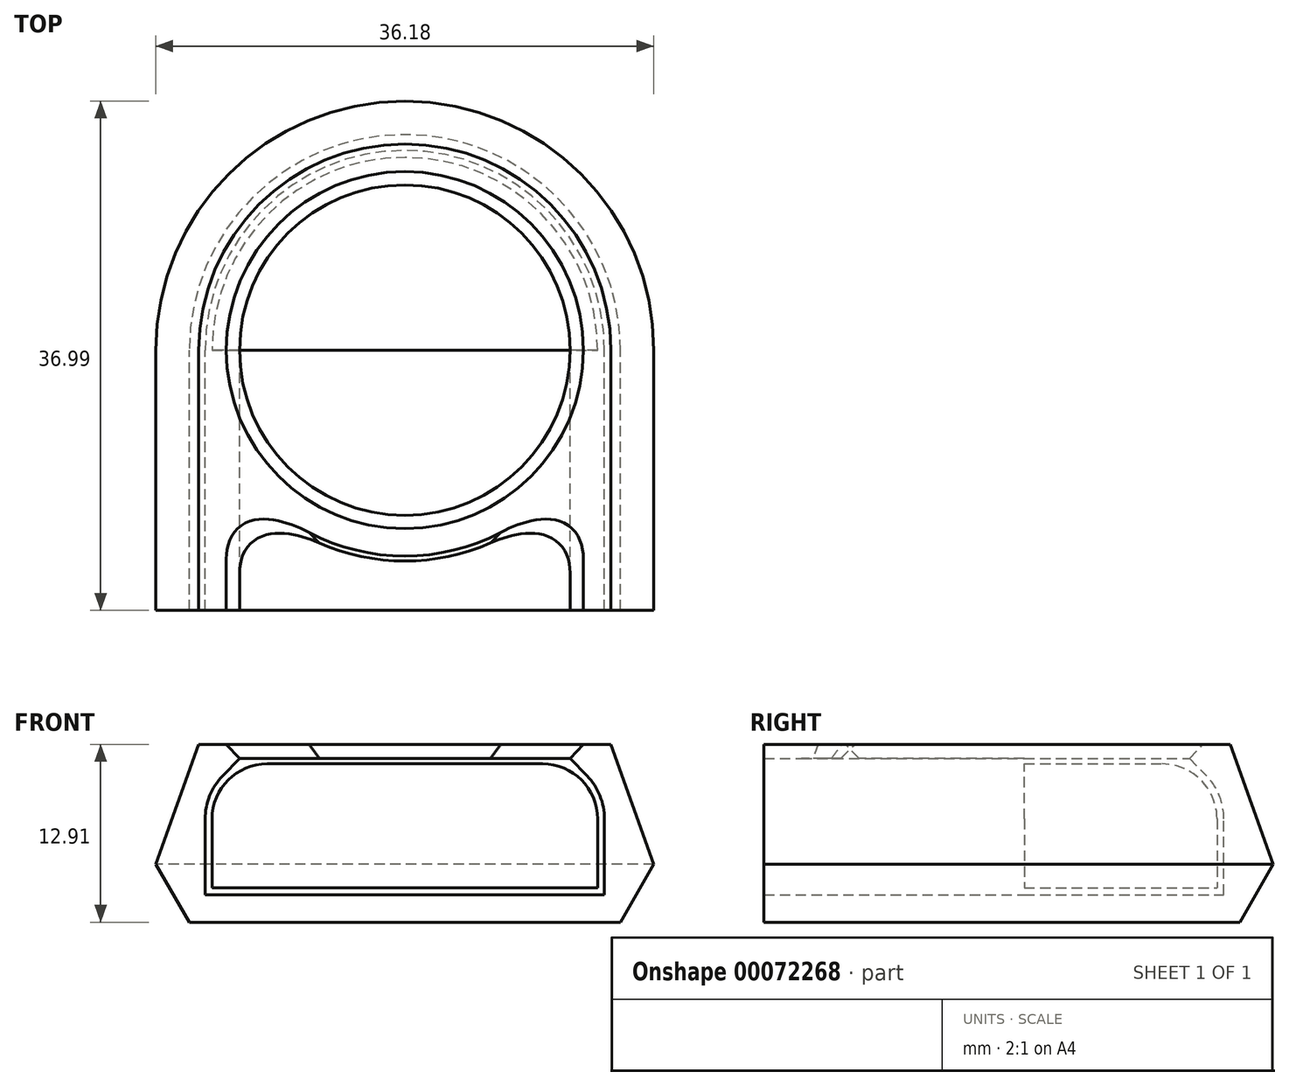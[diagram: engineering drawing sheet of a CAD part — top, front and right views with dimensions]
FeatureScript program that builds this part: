
annotation { "Feature Type Name" : "Feature", "Feature Type Description" : "" }
export const myFeature = defineFeature(function(context is Context, id is Id, definition is map)
    precondition{}
    {
        {
            var Q0;
            Q0=qCreatedBy(makeId("Top.planeOp"),FACE);
            var sketch = newSketch(context, id + "F0", { "sketchPlane" : qUnion([Q0])});
            skCircle(sketch, "E0", {"center": v(0, 0) * mm, "radius": 14 * mm});
            skSolve(sketch);
        }
        {
            var Q0;
            Q0=makeQuery(id+"F0.imprint","IMPRINT",FACE,{"disambiguationData":[TD([[makeQuery(id+"F0.imprint","IMPRINT",EDGE,{"derivedFrom":sQuery(id+"F0.wireOp",EDGE,"E0")}),1.0]])]});
            extrude(context, id + "F1", {"entities" : qUnion([Q0]), "depth" : 9 * mm});
        }
        {
            var Q0;
            Q0=makeQuery(id+"F1.opExtrude","CAP_EDGE",EDGE,{"disambiguationData":[OSD([sQuery(id+"F0.wireOp",EDGE,"E0")])],"isStart":false});
            fillet(context, id + "F2", {"entities" : qUnion([Q0]), "radius" : 4 * mm, "tangentPropagation" : true, "allowEdgeOverflow" : false});
        }
        {
            var Q0;
            Q0=qCreatedBy(makeId("Front.planeOp"),FACE);
            var sketch = newSketch(context, id + "F3", { "sketchPlane" : qUnion([Q0])});
            skLineSegment(sketch, "E1", {"start": v(0, -0.5) * mm, "end": v(-14.5, -0.5) * mm});
            skLineSegment(sketch, "E2", {"start": v(-14.5, -0.5) * mm, "end": v(-14.5, 5) * mm});
            skLineSegment(sketch, "E3", {"start": v(0, -0.5) * mm, "end": v(0, -2.5) * mm});
            skLineSegment(sketch, "E4", {"start": v(0, -2.5) * mm, "end": v(-15.65, -2.5) * mm});
            skLineSegment(sketch, "E5", {"start": v(-15.65, -2.5) * mm, "end": v(-18.09, 1.71) * mm});
            skLineSegment(sketch, "E6", {"start": v(-18.09, 1.71) * mm, "end": v(-14.97, 10.4) * mm});
            skLineSegment(sketch, "E7", {"start": v(-14.97, 10.4) * mm, "end": v(-12.97, 10.4) * mm});
            skArc(sketch, "E8", {"start": v(-13.24, 8.13) * mm, "mid": v(-14.17, 6.69) * mm, "end": v(-14.5, 5) * mm});
            skArc(sketch, "E9", {"start": v(-10, 9) * mm, "mid": v(-12.83, 7.83) * mm, "end": v(-14, 5) * mm});
            skLineSegment(sketch, "E10", {"start": v(-14, 0) * mm, "end": v(-14, 5) * mm});
            skLineSegment(sketch, "E11", {"start": v(-10, 9) * mm, "end": v(0, 9) * mm});
            skLineSegment(sketch, "E12", {"start": v(0, 9) * mm, "end": v(0, 0) * mm});
            skLineSegment(sketch, "E13", {"start": v(0, 0) * mm, "end": v(-14, 0) * mm});
            skLineSegment(sketch, "E14.MirrorCS", {"start": v(10, 9) * mm, "end": v(0, 9) * mm});
            skArc(sketch, "E15.MirrorCS", {"start": v(10, 9) * mm, "mid": v(12.83, 7.83) * mm, "end": v(14, 5) * mm});
            skLineSegment(sketch, "E16.MirrorCS", {"start": v(14, 0) * mm, "end": v(14, 5) * mm});
            skLineSegment(sketch, "E17.MirrorCS", {"start": v(0, 0) * mm, "end": v(14, 0) * mm});
            skLineSegment(sketch, "E18", {"start": v(-12.88, 7.78) * mm, "end": v(-8.73, 12.07) * mm, "construction": true});
            skLineSegment(sketch, "E19", {"start": v(-13.24, 8.13) * mm, "end": v(-12, 9.4) * mm});
            skLineSegment(sketch, "E20", {"start": v(-12, 9.4) * mm, "end": v(-12.97, 10.4) * mm});
            skLineSegment(sketch, "E21", {"start": v(-12.97, 10.4) * mm, "end": v(0, 10.4) * mm});
            skLineSegment(sketch, "E22", {"start": v(0, 10.4) * mm, "end": v(0, 9) * mm});
            skLineSegment(sketch, "E23", {"start": v(0, 0) * mm, "end": v(0, -0.5) * mm});
            skLineSegment(sketch, "E24", {"start": v(-12, 9.4) * mm, "end": v(0, 9.4) * mm});
            skLineSegment(sketch, "E25.MirrorCS", {"start": v(12, 9.4) * mm, "end": v(0, 9.4) * mm});
            skLineSegment(sketch, "E26.MirrorCS", {"start": v(12.97, 10.4) * mm, "end": v(0, 10.4) * mm});
            skLineSegment(sketch, "E27.MirrorCS", {"start": v(12, 9.4) * mm, "end": v(12.97, 10.4) * mm});
            skLineSegment(sketch, "E28.MirrorCS", {"start": v(13.24, 8.13) * mm, "end": v(12, 9.4) * mm});
            skArc(sketch, "E29.MirrorCS", {"start": v(13.24, 8.13) * mm, "mid": v(14.17, 6.69) * mm, "end": v(14.5, 5) * mm});
            skLineSegment(sketch, "E30.MirrorCS", {"start": v(14.5, -0.5) * mm, "end": v(14.5, 5) * mm});
            skLineSegment(sketch, "E31.MirrorCS", {"start": v(0, -0.5) * mm, "end": v(14.5, -0.5) * mm});
            skSolve(sketch);
        }
        {
            var Q0;
            Q0=makeQuery(id+"F3.imprint","IMPRINT",FACE,{"disambiguationData":[TD([[makeQuery(id+"F3.imprint","IMPRINT",EDGE,{"derivedFrom":sQuery(id+"F3.wireOp",EDGE,"E1")}),1.0]])]});
            var Q1;
            Q1=sQuery(id+"F3.wireOp",EDGE,"E12");
            revolve(context, id + "F4", {"entities" : qUnion([Q0]), "axis" : qUnion([Q1]), "revolveType" : RevolveType.ONE_DIRECTION, "angle" : 180 * degree});
        }
        {
            var Q0;
            Q0=makeQuery(id+"F4.opRevolve","CAP_FACE",FACE,{"disambiguationData":[OSD([sQuery(id+"F3.wireOp",EDGE,"E1"),sQuery(id+"F3.wireOp",EDGE,"E2"),sQuery(id+"F3.wireOp",EDGE,"E3"),sQuery(id+"F3.wireOp",EDGE,"E4"),sQuery(id+"F3.wireOp",EDGE,"E5"),sQuery(id+"F3.wireOp",EDGE,"E6"),sQuery(id+"F3.wireOp",EDGE,"E7"),sQuery(id+"F3.wireOp",EDGE,"E8"),sQuery(id+"F3.wireOp",EDGE,"E19"),sQuery(id+"F3.wireOp",EDGE,"E20")])],"isStart":false});
            extrude(context, id + "F5", {"entities" : qUnion([Q0]), "operationType" : NewBodyOperationType.ADD, "depth" : 18.9 * mm});
        }
        {
            var Q0;
            Q0=makeQuery(id+"F3.imprint","IMPRINT",FACE,{"disambiguationData":[TD([[makeQuery(id+"F3.imprint","IMPRINT",EDGE,{"derivedFrom":sQuery(id+"F3.wireOp",EDGE,"E1")}),1.0]])]});
            var Q1;
            Q1=sQuery(id+"F3.wireOp",EDGE,"E12");
            revolve(context, id + "F6", {"operationType" : NewBodyOperationType.ADD, "entities" : qUnion([Q0]), "axis" : qUnion([Q1]), "revolveType" : RevolveType.FULL});
        }
        {
            var Q0;
            Q0=makeQuery(id+"F3.imprint","IMPRINT",FACE,{"disambiguationData":[TD([[makeQuery(id+"F3.imprint","IMPRINT",EDGE,{"derivedFrom":sQuery(id+"F3.wireOp",EDGE,"E1")}),-1.0]])]});
            var Q1;
            Q1=makeQuery(id+"F3.imprint","IMPRINT",FACE,{"disambiguationData":[TD([[makeQuery(id+"F3.imprint","IMPRINT",EDGE,{"derivedFrom":sQuery(id+"F3.wireOp",EDGE,"E9")}),1.0]])]});
            var Q2;
            {var subQ1=sQuery(id+"F3.wireOp",EDGE,"E14.MirrorCS");Q2=makeQuery(id+"F3.imprint","IMPRINT",FACE,{"disambiguationData":[TD([[makeQuery(id+"F3.imprint","IMPRINT",EDGE,{"derivedFrom":subQ1}),-1.0]])]});}
            var Q3;
            Q3=makeQuery(id+"F3.imprint","IMPRINT",FACE,{"disambiguationData":[TD([[makeQuery(id+"F3.imprint","IMPRINT",EDGE,{"derivedFrom":sQuery(id+"F3.wireOp",EDGE,"E12")}),1.0]])]});
            extrude(context, id + "F7", {"entities" : qUnion([Q0, Q1, Q2, Q3]), "operationType" : NewBodyOperationType.REMOVE, "depth" : 25 * mm});
        }
        {
            var Q0;
            {var subQ0=sQuery(id+"F3.wireOp",EDGE,"E20");Q0=makeQuery(id+"F6.boolean.opBoolean","INTERSECT",EDGE,{"derivedFrom":[makeQuery(id+"F5.opExtrude","SWEPT_FACE",FACE,{"disambiguationData":[OSD([subQ0]),TDD([makeQuery(id+"F4.opRevolve","CAP_EDGE",EDGE,{"disambiguationData":[OSD([subQ0])],"isStart":true})])]}),makeQuery(id+"F6.opRevolve","SWEPT_FACE",FACE,{"disambiguationData":[OSD([sQuery(id+"F3.wireOp",EDGE,"E6")])]})]});}
            var Q1;
            {var subQ0=sQuery(id+"F3.wireOp",EDGE,"E20");Q1=makeQuery(id+"F6.boolean.opBoolean","INTERSECT",EDGE,{"derivedFrom":[makeQuery(id+"F5.opExtrude","SWEPT_FACE",FACE,{"disambiguationData":[OSD([subQ0]),TDD([makeQuery(id+"F4.opRevolve","CAP_EDGE",EDGE,{"disambiguationData":[OSD([subQ0])],"isStart":false})])]}),makeQuery(id+"F6.opRevolve","SWEPT_FACE",FACE,{"disambiguationData":[OSD([sQuery(id+"F3.wireOp",EDGE,"E6")])]})]});}
            fillet(context, id + "F8", {"entities" : qUnion([Q0, Q1]), "radius" : 4 * mm, "tangentPropagation" : true, "allowEdgeOverflow" : false});
        }
    });
